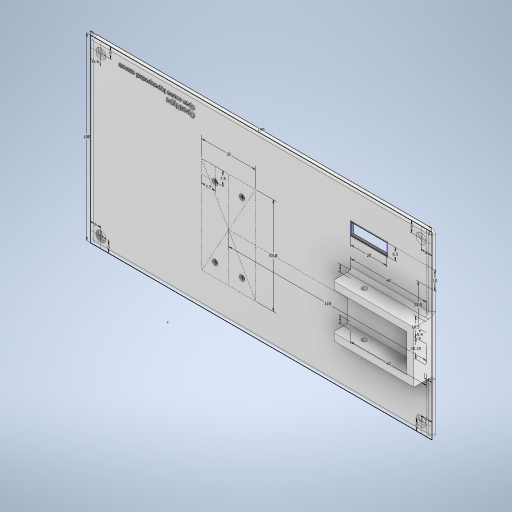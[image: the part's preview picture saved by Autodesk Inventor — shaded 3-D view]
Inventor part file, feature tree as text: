
AUTODESK INVENTOR PART (.ipt)
format: ipt  version: 2023 (Build 270158000, 158)  size: 1,290,240 bytes
history: native  units: mm
features: extrude x7, fillet x6, sketch x3, hole x2
ambient origin geometry x8: Origin, YZ Plane, XZ Plane, XY Plane, X Axis, Y Axis, Z Axis, Center Point
bodies: Solid1 (feature_tree)
feature tree (18):
  sketch  "Sketch1"  dims[d0=190.0mm d1=100.0mm]
  extrude  "Extrusion1"  Depth=100.0mm
  extrude  "Extrusion2"  Depth=5.4mm
  extrude  "Extrusion3"  Depth=0.5mm
  hole  "Hole1"  [1 undecoded]
  extrude  "Extrusion4"  Depth=0.5mm
  hole  "Hole2"  [1 undecoded]
  fillet  "Fillet1"  Radius=4.0mm
  fillet  "Fillet2"  Radius=4.0mm
  fillet  "Fillet3"  Radius=10.0mm
  fillet  "Fillet4"  Radius=12.5mm
  extrude  "Extrusion5"  Depth=0.5mm
  extrude  "Extrusion6"  Depth=0.5mm
  fillet  "Fillet5"  Radius=30.0mm
  extrude  "Extrusion7"  Depth=2.0mm TaperAngle=0.0deg
  fillet  "Fillet6"  Radius=110.0mm
  sketch  "Sketch2"  dims[d2=3.0mm d14=5.4mm]
  sketch  "Sketch3"  dims[d15=10.25mm d16=42.0mm d17=4.0mm d18=10.5mm d19=42.0mm d20=4.0mm d21=4.0mm d22=10.0mm d23=0.0mm d24=12.5mm d25=5.0mm d26=2.7mm d27=30.0mm d28=0.0mm d29=2.0mm d30=0.0mm d31=110.0mm d32=30.0mm d33=53.8mm d34=7.5mm d35=7.5mm d36=3.0mm d37=6.0mm d38=19.05mm d39=4.775mm d40=90.0deg d41=5.0mm d42=20.594885mm d43=20.0mm d44=3.5mm d45=150.0mm d46=3.0mm d47=50.0mm d48=3.5mm d49=20.0mm d50=3.0mm d51=60.0mm d52=50.0mm d53=90.0deg d54=20.0mm d55=3.5mm d56=3.5mm d57=20.0mm d58=150.0mm d59=3.0mm d60=3.5mm d61=60.0mm d62=2.0mm d63=0.0mm d64=6.0mm d65=6.0mm d66=6.0mm d67=6.0mm d68=6.0mm d69=6.0mm d70=6.0mm d71=6.0mm d72=3.0mm d73=6.0mm d74=5.5mm d75=1.5mm d76=90.0deg d77=5.0mm d78=20.594885mm d79=2.0mm d80=2.0mm d81=1.0mm d82=1.0mm d83=1.8mm d84=0.0mm d85=22.5mm d86=10.0mm d87=20.0mm d88=6.5mm d89=10.0mm d90=0.0mm d91=2.0mm d92=0.5mm d93=0.0mm d94=0.5mm]
note: 2 required parameter values undecoded (feature->parameter linkage not recoverable at this tier; creation-order binding heuristic only, values carry confidence <= 0.55)
